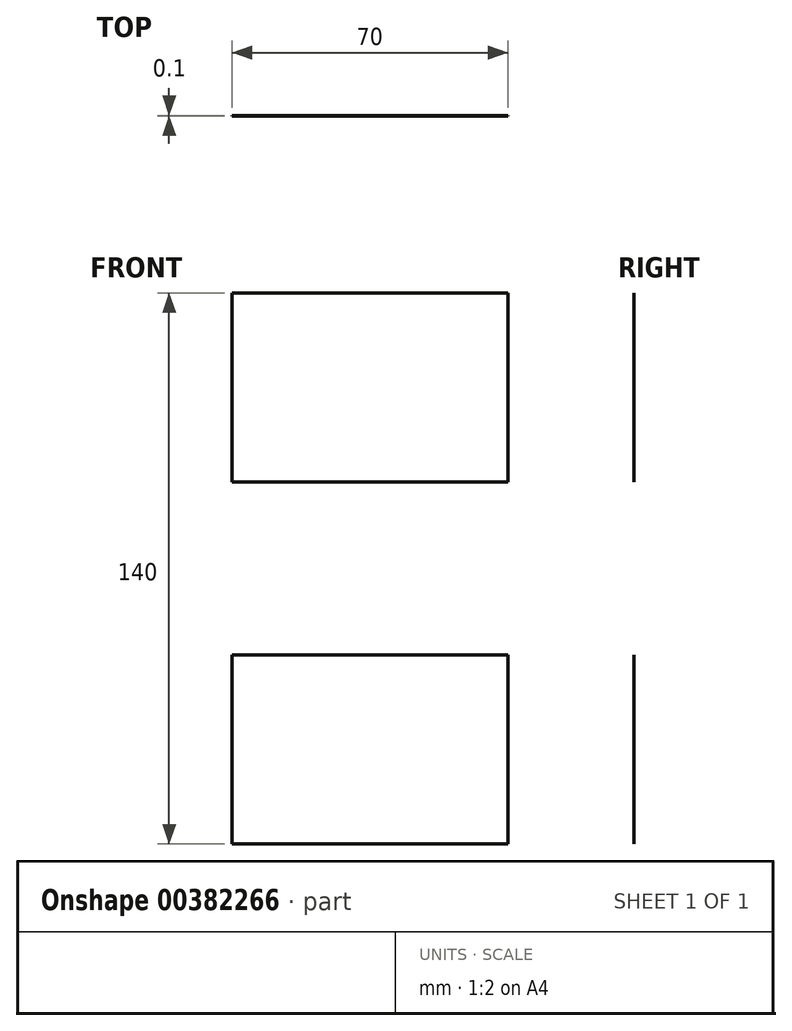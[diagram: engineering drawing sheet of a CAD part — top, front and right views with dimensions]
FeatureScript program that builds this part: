
annotation { "Feature Type Name" : "Feature", "Feature Type Description" : "" }
export const myFeature = defineFeature(function(context is Context, id is Id, definition is map)
    precondition{}
    {
        {
            var Q0;
            Q0=qCreatedBy(makeId("Front.planeOp"),FACE);
            var sketch = newSketch(context, id + "F0", { "sketchPlane" : qUnion([Q0])});
            skLineSegment(sketch, "E0", {"start": v(-79.5, 0) * mm, "end": v(86.28, 0) * mm});
            skPoint(sketch, "E1", {"position": v(0, 0) * mm});
            skPoint(sketch, "E2", {"position": v(0, -15) * mm});
            skPoint(sketch, "E3", {"position": v(0, -22) * mm});
            skPoint(sketch, "E4", {"position": v(0, -70) * mm});
            skPoint(sketch, "E5", {"position": v(0, -46) * mm});
            skPoint(sketch, "E6", {"position": v(35, -46) * mm});
            skLineSegment(sketch, "E7", {"start": v(0, 0) * mm, "end": v(0, -70) * mm});
            skPoint(sketch, "E8.MirrorP", {"position": v(-35, -46) * mm});
            skPoint(sketch, "E9", {"position": v(35, -22) * mm});
            skPoint(sketch, "E10", {"position": v(-35, -22) * mm});
            skPoint(sketch, "E11", {"position": v(-35, -70) * mm});
            skPoint(sketch, "E12", {"position": v(35, -70) * mm});
            skLineSegment(sketch, "E13", {"start": v(-35, -22) * mm, "end": v(35, -22) * mm});
            skLineSegment(sketch, "E14", {"start": v(35, -22) * mm, "end": v(35, -70) * mm});
            skLineSegment(sketch, "E15", {"start": v(-35, -70) * mm, "end": v(35, -70) * mm});
            skLineSegment(sketch, "E16", {"start": v(-35, -22) * mm, "end": v(-35, -70) * mm});
            skLineSegment(sketch, "E17.MirrorCS", {"start": v(35, 22) * mm, "end": v(35, 70) * mm});
            skLineSegment(sketch, "E18.MirrorCS", {"start": v(-35, 22) * mm, "end": v(-35, 70) * mm});
            skPoint(sketch, "E19.MirrorP", {"position": v(0, 22) * mm});
            skLineSegment(sketch, "E20.MirrorCS", {"start": v(-35, 22) * mm, "end": v(35, 22) * mm});
            skLineSegment(sketch, "E21.MirrorCS", {"start": v(-35, 70) * mm, "end": v(35, 70) * mm});
            skSolve(sketch);
        }
        {
            var Q0;
            Q0=makeQuery(id+"F0.imprint","IMPRINT",FACE,{"disambiguationData":[TD([[makeQuery(id+"F0.imprint","IMPRINT",EDGE,{"derivedFrom":sQuery(id+"F0.wireOp",EDGE,"E17.MirrorCS")}),1.0]])]});
            var Q1;
            {var subQ5=sQuery(id+"F0.wireOp",EDGE,"E14");Q1=makeQuery(id+"F0.imprint","IMPRINT",FACE,{"disambiguationData":[TD([[makeQuery(id+"F0.imprint","IMPRINT",EDGE,{"derivedFrom":subQ5}),-1.0]])]});}
            var Q2;
            {var subQ5=sQuery(id+"F0.wireOp",EDGE,"E16");Q2=makeQuery(id+"F0.imprint","IMPRINT",FACE,{"disambiguationData":[TD([[makeQuery(id+"F0.imprint","IMPRINT",EDGE,{"derivedFrom":subQ5}),1.0]])]});}
            extrude(context, id + "F1", {"entities" : qUnion([Q0, Q1, Q2]), "depth" : 0.1 * mm});
        }
    });
